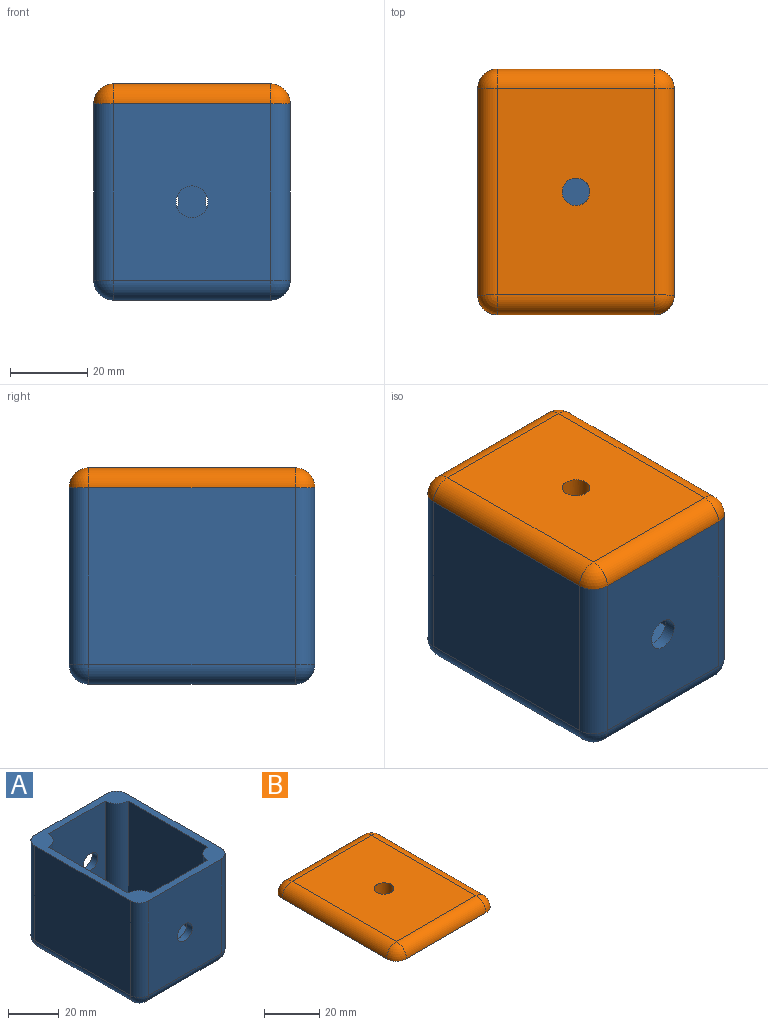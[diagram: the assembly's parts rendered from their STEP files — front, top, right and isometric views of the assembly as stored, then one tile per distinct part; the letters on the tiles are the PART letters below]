
ASSEMBLY  parts=2 mates=1
PART A: 30 faces, bbox 50.8x63.5x50.8 mm
  f0: plane 44.45x44.45mm, normal (-1,0,0), area 1975.8mm2, adj f4,f10,f14,f15
  f1: plane 44.45x31.75mm, normal (0,-1,0), area 1304.2mm2, adj f4,f10,f13,f14,f16,f17
  f2: plane 44.45x44.45mm, normal (1,0,0), area 1975.8mm2, adj f4,f10,f12,f13
  f3: plane 44.45x31.75mm, normal (0,1,0), area 1357.8mm2, adj f4,f10,f11,f12,f15
  f4: plane 63.5x50.8mm, normal (0,0,1), area 790mm2, adj f0,f1,f2,f3,f5,f6,f7,f8
  f5: plane 53.34x45.72mm, normal (1,0,0), area 2438.7mm2, adj f4,f23,f27,f29
  f6: plane 45.72x40.64mm, normal (0,1,0), area 1751mm2, adj f4,f16,f17,f20,f26,f29
  f7: plane 53.34x45.72mm, normal (-1,0,0), area 2438.7mm2, adj f4,f18,f20,f21
  f8: plane 45.72x40.64mm, normal (0,-1,0), area 1804.5mm2, adj f4,f11,f18,f22,f23
  f9: plane 53.34x40.64mm, normal (0,0,-1), area 2167.7mm2, adj f21,f22,f26,f27
  f10: plane 57.15x44.45mm, normal (0,0,1), area 2413.6mm2, adj f0,f1,f2,f3,f12,f13,f14,f15
  f11: cylinder r=4.13mm len=8.26mm, axis (0,-1,0), area 82.3mm2, adj f3,f8
  f12: cylinder r=6.35mm len=44.45mm, axis (0,0,1), area 443.4mm2, adj f2,f3,f4,f10
  f13: cylinder r=6.35mm len=44.45mm, axis (0,0,1), area 443.4mm2, adj f1,f2,f4,f10
  f14: cylinder r=6.35mm len=44.45mm, axis (0,0,1), area 443.4mm2, adj f0,f1,f4,f10
  f15: cylinder r=6.35mm len=44.45mm, axis (0,0,1), area 443.4mm2, adj f0,f3,f4,f10
  f16: cylinder r=4.13mm len=8.26mm, axis (0,1,0), area 82.3mm2, adj f1,f6
  f17: cylinder r=4.13mm len=8.26mm, axis (0,1,0), area 82.3mm2, adj f1,f6
  f18: cylinder r=5.08mm len=45.72mm, axis (0,0,1), area 364.8mm2, adj f4,f7,f8,f19
  f19: sphere r=5.08mm, area 40.5mm2, adj f18,f21,f22
  f20: cylinder r=5.08mm len=45.72mm, axis (0,0,-1), area 364.8mm2, adj f4,f6,f7,f24
  f21: cylinder r=5.08mm len=53.34mm, axis (0,-1,0), area 425.6mm2, adj f7,f9,f19,f24
  f22: cylinder r=5.08mm len=40.64mm, axis (1,0,0), area 324.3mm2, adj f8,f9,f19,f25
  f23: cylinder r=5.08mm len=45.72mm, axis (0,0,-1), area 364.8mm2, adj f4,f5,f8,f25
  f24: sphere r=5.08mm, area 40.5mm2, adj f20,f21,f26
  f25: sphere r=5.08mm, area 40.5mm2, adj f22,f23,f27
  f26: cylinder r=5.08mm len=40.64mm, axis (-1,0,0), area 324.3mm2, adj f6,f9,f24,f28
  f27: cylinder r=5.08mm len=53.34mm, axis (0,1,0), area 425.6mm2, adj f5,f9,f25,f28
  f28: sphere r=5.08mm, area 40.5mm2, adj f26,f27,f29
  f29: cylinder r=5.08mm len=45.72mm, axis (0,0,1), area 364.8mm2, adj f4,f5,f6,f28
PART B: 15 faces, bbox 50.8x63.5x5.1 mm
  f0: plane 2.54x1.91mm, normal (0,1,0), area 4.8mm2, adj f1,f3,f4,f6
  f1: plane 4.64x2.54mm, normal (-1,0,0), area 11.8mm2, adj f0,f2,f4,f6
  f2: cylinder r=3.56mm len=7.11mm, axis (0,0,1), area 108.6mm2, adj f1,f3,f4,f5,f6
  f3: plane 4.64x2.54mm, normal (1,0,0), area 11.8mm2, adj f0,f2,f4,f6
  f4: plane 63.5x50.8mm, normal (0,0,-1), area 3155.2mm2, adj f0,f1,f2,f3,f7,f8,f9,f10
  f5: plane 53.34x40.64mm, normal (0,0,1), area 2128mm2, adj f2,f8,f9,f12,f13
  f6: plane 4.64x1.91mm, normal (0,0,-1), area 8.7mm2, adj f0,f1,f2,f3
  f7: sphere r=5.08mm, area 40.5mm2, adj f4,f8,f9
  f8: cylinder r=5.08mm len=53.34mm, axis (0,1,0), area 425.6mm2, adj f4,f5,f7,f10
  f9: cylinder r=5.08mm len=40.64mm, axis (1,0,0), area 324.3mm2, adj f4,f5,f7,f11
  f10: sphere r=5.08mm, area 40.5mm2, adj f4,f8,f12
  f11: sphere r=5.08mm, area 40.5mm2, adj f4,f9,f13
  f12: cylinder r=5.08mm len=40.64mm, axis (-1,0,0), area 324.3mm2, adj f4,f5,f10,f14
  f13: cylinder r=5.08mm len=53.34mm, axis (0,-1,0), area 425.6mm2, adj f4,f5,f11,f14
  f14: sphere r=5.08mm, area 40.5mm2, adj f4,f12,f13
PLACE A t=(42.48,41.55,43.73)mm
PLACE B t=(42.48,-21.95,89.45)mm
MATE fastened A.f29 <-> B.f4  axis (0,0,1) through (62.8,68.22,94.53)mm
